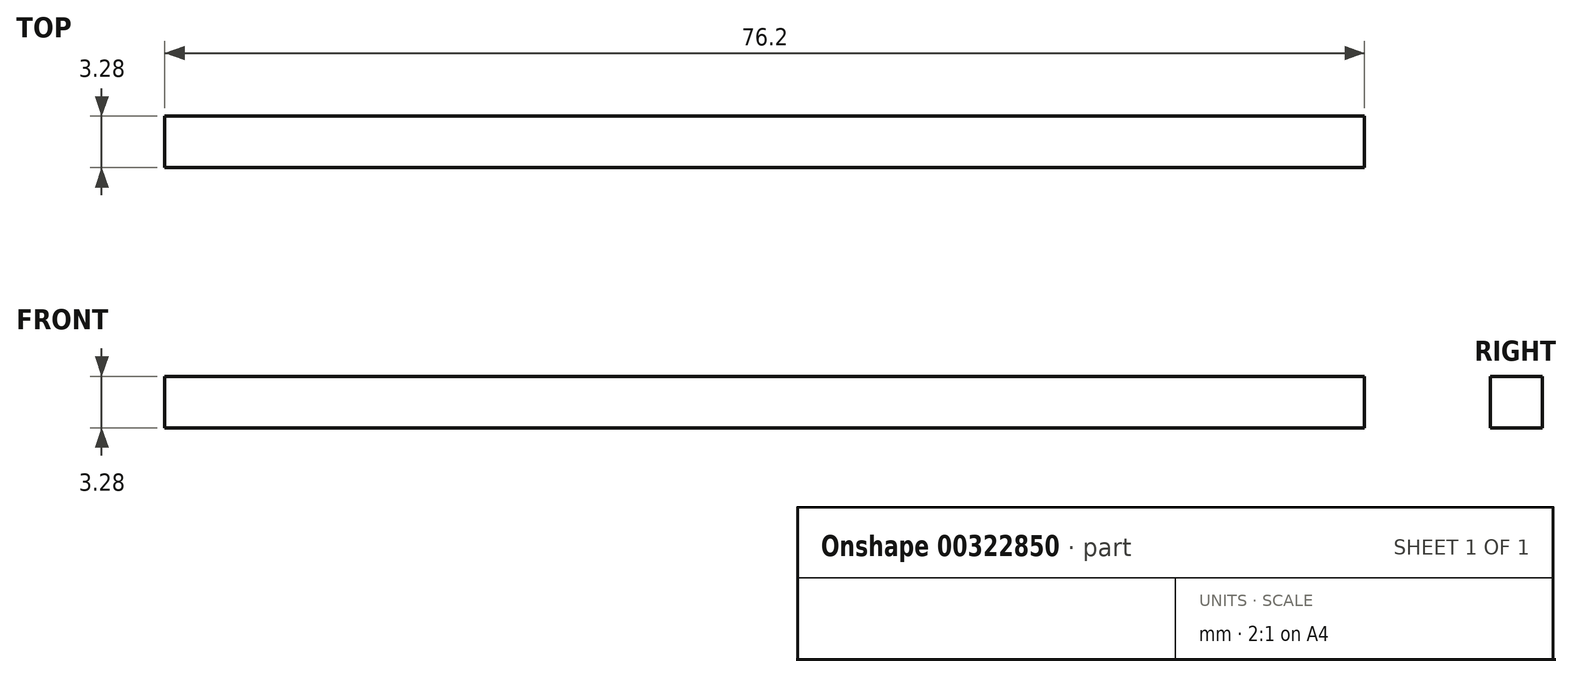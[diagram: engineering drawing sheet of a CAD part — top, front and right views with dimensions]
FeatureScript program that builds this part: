
annotation { "Feature Type Name" : "Feature", "Feature Type Description" : "" }
export const myFeature = defineFeature(function(context is Context, id is Id, definition is map)
    precondition{}
    {
        {
            var Q0;
            Q0=qCreatedBy(makeId("Right.planeOp"),FACE);
            var sketch = newSketch(context, id + "F0", { "sketchPlane" : qUnion([Q0])});
            skLineSegment(sketch, "E0.bottom", {"start": v(1.64, -1.64) * mm, "end": v(-1.64, -1.64) * mm});
            skLineSegment(sketch, "E0.top", {"start": v(1.64, 1.64) * mm, "end": v(-1.64, 1.64) * mm});
            skLineSegment(sketch, "E0.left", {"start": v(1.64, -1.64) * mm, "end": v(1.64, 1.64) * mm});
            skLineSegment(sketch, "E0.right", {"start": v(-1.64, -1.64) * mm, "end": v(-1.64, 1.64) * mm});
            skPoint(sketch, "E0.middle", {"position": v(0, 0) * mm});
            skSolve(sketch);
        }
        {
            var Q0;
            Q0=qSketchRegion(id+"F0",true);
            extrude(context, id + "F1", {"entities" : qUnion([Q0]), "depth" : 76.2 * mm});
        }
    });
